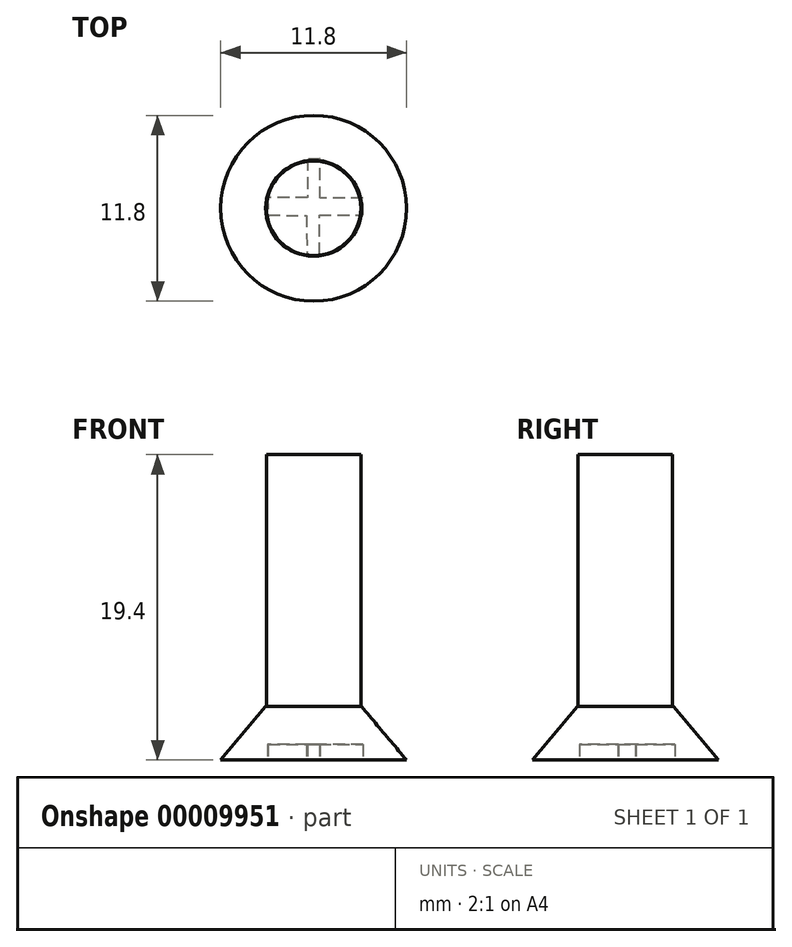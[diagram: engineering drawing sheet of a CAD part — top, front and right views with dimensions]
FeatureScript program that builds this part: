
annotation { "Feature Type Name" : "Feature", "Feature Type Description" : "" }
export const myFeature = defineFeature(function(context is Context, id is Id, definition is map)
    precondition{}
    {
        {
            var Q0;
            Q0=qCreatedBy(makeId("Top.planeOp"),FACE);
            var sketch = newSketch(context, id + "F0", { "sketchPlane" : qUnion([Q0])});
            skCircle(sketch, "E0", {"center": v(0, 0) * mm, "radius": 5.9 * mm});
            skSolve(sketch);
        }
        {
            var Q0;
            Q0 = qSketchRegion(id + "F0", true);
            extrude(context, id + "F1", {"entities" : qUnion([Q0]), "depth" : 3.4 * mm, "hasDraft" : true, "draftAngle" : 40 * degree, "draftPullDirection" : true});
        }
        {
            var Q0;
            Q0=makeQuery(id+"F1.opExtrude","CAP_FACE",FACE,{"disambiguationData":[OSD([sQuery(id+"F0.wireOp",EDGE,"E0")])],"isStart":false});
            var sketch = newSketch(context, id + "F2", { "sketchPlane" : qUnion([Q0])});
            skCircle(sketch, "E1", {"center": v(0, 0) * mm, "radius": 3 * mm});
            skSolve(sketch);
        }
        {
            var Q0;
            Q0 = qSketchRegion(id + "F2", true);
            extrude(context, id + "F3", {"entities" : qUnion([Q0]), "operationType" : NewBodyOperationType.ADD, "depth" : 16 * mm});
        }
        {
            var Q0;
            Q0=makeQuery(id+"F1.opExtrude","CAP_FACE",FACE,{"disambiguationData":[OSD([sQuery(id+"F0.wireOp",EDGE,"E0")])],"isStart":true});
            var sketch = newSketch(context, id + "F4", { "sketchPlane" : qUnion([Q0])});
            skLineSegment(sketch, "E2", {"start": v(-0.41, 2.93) * mm, "end": v(0.37, 2.93) * mm});
            skLineSegment(sketch, "E3", {"start": v(0.37, 2.93) * mm, "end": v(0.37, 0.44) * mm});
            skLineSegment(sketch, "E4", {"start": v(0.37, 0.44) * mm, "end": v(3.13, 0.44) * mm});
            skLineSegment(sketch, "E5", {"start": v(3.13, 0.44) * mm, "end": v(3.13, -0.64) * mm});
            skLineSegment(sketch, "E6", {"start": v(3.13, -0.64) * mm, "end": v(0.41, -0.64) * mm});
            skLineSegment(sketch, "E7", {"start": v(0.41, -0.64) * mm, "end": v(0.41, -3.16) * mm});
            skLineSegment(sketch, "E8", {"start": v(0.41, -3.16) * mm, "end": v(-0.4, -3.13) * mm});
            skLineSegment(sketch, "E9", {"start": v(-0.4, -3.13) * mm, "end": v(-0.4, -0.69) * mm});
            skLineSegment(sketch, "E10", {"start": v(-0.4, -0.69) * mm, "end": v(-2.93, -0.69) * mm});
            skLineSegment(sketch, "E11", {"start": v(-2.93, -0.69) * mm, "end": v(-2.88, 0.44) * mm});
            skLineSegment(sketch, "E12", {"start": v(-2.88, 0.44) * mm, "end": v(-0.46, 0.46) * mm});
            skLineSegment(sketch, "E13", {"start": v(-0.46, 0.46) * mm, "end": v(-0.41, 2.93) * mm});
            skSolve(sketch);
        }
        {
            var Q0;
            Q0 = qSketchRegion(id + "F4", true);
            extrude(context, id + "F5", {"entities" : qUnion([Q0]), "operationType" : NewBodyOperationType.REMOVE, "oppositeDirection" : true, "depth" : 1 * mm});
        }
    });
